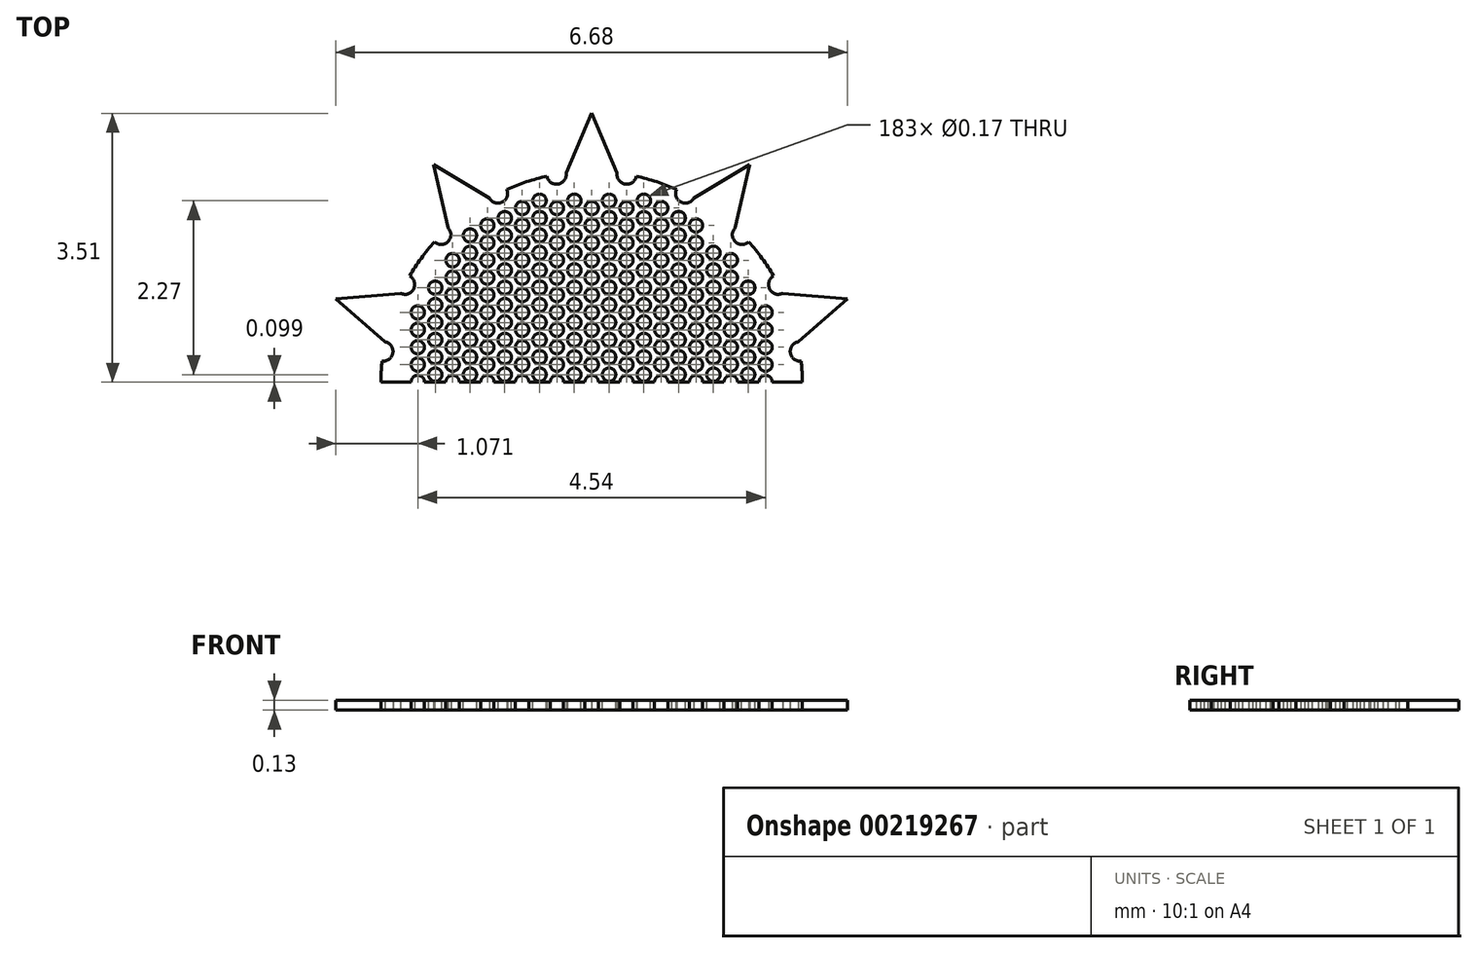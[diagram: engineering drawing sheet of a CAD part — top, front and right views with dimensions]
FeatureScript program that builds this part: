
annotation { "Feature Type Name" : "Feature", "Feature Type Description" : "" }
export const myFeature = defineFeature(function(context is Context, id is Id, definition is map)
    precondition{}
    {
        {
            var Q0;
            Q0=qCreatedBy(makeId("Top.planeOp"),FACE);
            var sketch = newSketch(context, id + "F0", { "sketchPlane" : qUnion([Q0])});
            skCircle(sketch, "E0", {"center": v(0, 0) * mm, "radius": 2.5 * mm});
            skArc(sketch, "E1", {"start": v(0.33, 2.73) * mm, "mid": v(0, 2.75) * mm, "end": v(-0.33, 2.73) * mm});
            skPoint(sketch, "E2", {"position": v(0, 2.75) * mm});
            skLineSegment(sketch, "E3", {"start": v(-3.94, 3.51) * mm, "end": v(3.7, 3.51) * mm, "construction": true});
            skLineSegment(sketch, "E4", {"start": v(0, 3.51) * mm, "end": v(-0.33, 2.73) * mm});
            skLineSegment(sketch, "E5", {"start": v(0, 3.51) * mm, "end": v(0.33, 2.73) * mm});
            skLineSegment(sketch, "E6.1.0", {"start": v(-2.06, 2.84) * mm, "end": v(-1.87, 2.01) * mm});
            skLineSegment(sketch, "E6.1.1", {"start": v(-2.06, 2.84) * mm, "end": v(-1.34, 2.4) * mm});
            skLineSegment(sketch, "E6.2.0", {"start": v(-3.34, 1.09) * mm, "end": v(-2.7, 0.53) * mm});
            skLineSegment(sketch, "E6.2.1", {"start": v(-3.34, 1.09) * mm, "end": v(-2.5, 1.16) * mm});
            skLineSegment(sketch, "E6.3.0", {"start": v(-3.34, -1.09) * mm, "end": v(-2.5, -1.16) * mm});
            skLineSegment(sketch, "E6.3.1", {"start": v(-3.34, -1.09) * mm, "end": v(-2.7, -0.53) * mm});
            skLineSegment(sketch, "E6.4.0", {"start": v(-2.06, -2.84) * mm, "end": v(-1.34, -2.4) * mm});
            skLineSegment(sketch, "E6.4.1", {"start": v(-2.06, -2.84) * mm, "end": v(-1.87, -2.01) * mm});
            skLineSegment(sketch, "E6.5.0", {"start": v(0, -3.51) * mm, "end": v(0.33, -2.73) * mm});
            skLineSegment(sketch, "E6.5.1", {"start": v(0, -3.51) * mm, "end": v(-0.33, -2.73) * mm});
            skLineSegment(sketch, "E6.6.0", {"start": v(2.06, -2.84) * mm, "end": v(1.87, -2.01) * mm});
            skLineSegment(sketch, "E6.6.1", {"start": v(2.06, -2.84) * mm, "end": v(1.34, -2.4) * mm});
            skLineSegment(sketch, "E6.7.0", {"start": v(3.34, -1.09) * mm, "end": v(2.7, -0.53) * mm});
            skLineSegment(sketch, "E6.7.1", {"start": v(3.34, -1.09) * mm, "end": v(2.5, -1.16) * mm});
            skLineSegment(sketch, "E6.8.0", {"start": v(3.34, 1.09) * mm, "end": v(2.5, 1.16) * mm});
            skLineSegment(sketch, "E6.8.1", {"start": v(3.34, 1.09) * mm, "end": v(2.7, 0.53) * mm});
            skLineSegment(sketch, "E6.9.0", {"start": v(2.06, 2.84) * mm, "end": v(1.34, 2.4) * mm});
            skLineSegment(sketch, "E6.9.1", {"start": v(2.06, 2.84) * mm, "end": v(1.87, 2.01) * mm});
            skCircle(sketch, "E7", {"center": v(0, 0) * mm, "radius": 2.62 * mm});
            skPoint(sketch, "E8", {"position": v(0.46, 2.71) * mm});
            skArc(sketch, "E9", {"start": v(0.33, 2.73) * mm, "mid": v(0.44, 2.59) * mm, "end": v(0.58, 2.69) * mm});
            skArc(sketch, "E10.1.0", {"start": v(-1.34, 2.4) * mm, "mid": v(-1.17, 2.35) * mm, "end": v(-1.1, 2.52) * mm});
            skArc(sketch, "E10.2.0", {"start": v(-2.5, 1.16) * mm, "mid": v(-2.32, 1.21) * mm, "end": v(-2.38, 1.38) * mm});
            skArc(sketch, "E10.3.0", {"start": v(-2.7, -0.53) * mm, "mid": v(-2.6, -0.38) * mm, "end": v(-2.74, -0.28) * mm});
            skArc(sketch, "E10.4.0", {"start": v(-1.87, -2.01) * mm, "mid": v(-1.87, -1.84) * mm, "end": v(-2.05, -1.83) * mm});
            skArc(sketch, "E10.5.0", {"start": v(-0.33, -2.73) * mm, "mid": v(-0.44, -2.59) * mm, "end": v(-0.58, -2.69) * mm});
            skArc(sketch, "E10.6.0", {"start": v(1.34, -2.4) * mm, "mid": v(1.17, -2.35) * mm, "end": v(1.1, -2.52) * mm});
            skArc(sketch, "E10.7.0", {"start": v(2.5, -1.16) * mm, "mid": v(2.32, -1.21) * mm, "end": v(2.38, -1.38) * mm});
            skArc(sketch, "E10.8.0", {"start": v(2.7, 0.53) * mm, "mid": v(2.6, 0.38) * mm, "end": v(2.74, 0.28) * mm});
            skArc(sketch, "E10.9.0", {"start": v(1.87, 2.01) * mm, "mid": v(1.87, 1.84) * mm, "end": v(2.05, 1.83) * mm});
            skArc(sketch, "E11", {"start": v(-0.58, 2.69) * mm, "mid": v(-0.44, 2.59) * mm, "end": v(-0.33, 2.73) * mm});
            skArc(sketch, "E12.trimOffspring", {"start": v(-0.58, 2.69) * mm, "mid": v(-0.85, 2.62) * mm, "end": v(-1.1, 2.52) * mm});
            skArc(sketch, "E13.1.0", {"start": v(-2.05, 1.83) * mm, "mid": v(-1.87, 1.84) * mm, "end": v(-1.87, 2.01) * mm});
            skArc(sketch, "E13.2.0", {"start": v(-2.74, 0.28) * mm, "mid": v(-2.6, 0.38) * mm, "end": v(-2.7, 0.53) * mm});
            skArc(sketch, "E13.3.0", {"start": v(-2.38, -1.38) * mm, "mid": v(-2.32, -1.21) * mm, "end": v(-2.5, -1.16) * mm});
            skArc(sketch, "E13.4.0", {"start": v(-1.1, -2.52) * mm, "mid": v(-1.17, -2.35) * mm, "end": v(-1.34, -2.4) * mm});
            skArc(sketch, "E13.5.0", {"start": v(0.58, -2.69) * mm, "mid": v(0.44, -2.59) * mm, "end": v(0.33, -2.73) * mm});
            skArc(sketch, "E13.6.0", {"start": v(2.05, -1.83) * mm, "mid": v(1.87, -1.84) * mm, "end": v(1.87, -2.01) * mm});
            skArc(sketch, "E13.7.0", {"start": v(2.74, -0.28) * mm, "mid": v(2.6, -0.38) * mm, "end": v(2.7, -0.53) * mm});
            skArc(sketch, "E13.8.0", {"start": v(2.38, 1.38) * mm, "mid": v(2.32, 1.21) * mm, "end": v(2.5, 1.16) * mm});
            skArc(sketch, "E13.9.0", {"start": v(1.1, 2.52) * mm, "mid": v(1.17, 2.35) * mm, "end": v(1.34, 2.4) * mm});
            skArc(sketch, "E14.trimOffspring", {"start": v(1.1, 2.52) * mm, "mid": v(0.85, 2.62) * mm, "end": v(0.58, 2.69) * mm});
            skArc(sketch, "E15.trimOffspring", {"start": v(1.87, 2.01) * mm, "mid": v(1.62, 2.22) * mm, "end": v(1.34, 2.4) * mm});
            skArc(sketch, "E16.trimOffspring", {"start": v(2.38, 1.38) * mm, "mid": v(2.22, 1.62) * mm, "end": v(2.05, 1.83) * mm});
            skArc(sketch, "E17.trimOffspring", {"start": v(2.7, 0.53) * mm, "mid": v(2.62, 0.85) * mm, "end": v(2.5, 1.16) * mm});
            skArc(sketch, "E18.trimOffspring", {"start": v(2.74, -0.28) * mm, "mid": v(2.75, 0) * mm, "end": v(2.74, 0.28) * mm});
            skArc(sketch, "E19.trimOffspring", {"start": v(2.5, -1.16) * mm, "mid": v(2.62, -0.85) * mm, "end": v(2.7, -0.53) * mm});
            skArc(sketch, "E20.trimOffspring", {"start": v(2.05, -1.83) * mm, "mid": v(2.22, -1.62) * mm, "end": v(2.38, -1.38) * mm});
            skArc(sketch, "E21.trimOffspring", {"start": v(1.34, -2.4) * mm, "mid": v(1.62, -2.22) * mm, "end": v(1.87, -2.01) * mm});
            skArc(sketch, "E22.trimOffspring", {"start": v(-2.38, -1.38) * mm, "mid": v(-2.22, -1.62) * mm, "end": v(-2.05, -1.83) * mm});
            skArc(sketch, "E23.trimOffspring", {"start": v(-1.87, -2.01) * mm, "mid": v(-1.62, -2.22) * mm, "end": v(-1.34, -2.4) * mm});
            skArc(sketch, "E24.trimOffspring", {"start": v(-1.1, -2.52) * mm, "mid": v(-0.85, -2.62) * mm, "end": v(-0.58, -2.69) * mm});
            skArc(sketch, "E25.trimOffspring", {"start": v(-0.33, -2.73) * mm, "mid": v(0, -2.75) * mm, "end": v(0.33, -2.73) * mm});
            skArc(sketch, "E26.trimOffspring", {"start": v(0.58, -2.69) * mm, "mid": v(0.85, -2.62) * mm, "end": v(1.1, -2.52) * mm});
            skArc(sketch, "E27.trimOffspring", {"start": v(-2.7, -0.53) * mm, "mid": v(-2.62, -0.85) * mm, "end": v(-2.5, -1.16) * mm});
            skArc(sketch, "E28.trimOffspring", {"start": v(-2.74, 0.28) * mm, "mid": v(-2.75, 0) * mm, "end": v(-2.74, -0.28) * mm});
            skArc(sketch, "E29.trimOffspring", {"start": v(-2.5, 1.16) * mm, "mid": v(-2.62, 0.85) * mm, "end": v(-2.7, 0.53) * mm});
            skArc(sketch, "E30.trimOffspring", {"start": v(-2.05, 1.83) * mm, "mid": v(-2.22, 1.62) * mm, "end": v(-2.38, 1.38) * mm});
            skArc(sketch, "E31.trimOffspring", {"start": v(-1.34, 2.4) * mm, "mid": v(-1.62, 2.22) * mm, "end": v(-1.87, 2.01) * mm});
            skSolve(sketch);
        }
        {
            var Q0;
            Q0=qSketchRegion(id+"F0",true);
            var Q1;
            Q1=makeQuery(id+"F0.imprint","IMPRINT",FACE,{"disambiguationData":[TD([[makeQuery(id+"F0.imprint","IMPRINT",EDGE,{"derivedFrom":sQuery(id+"F0.wireOp",EDGE,"E0")}),1.0]])]});
            extrude(context, id + "F1", {"entities" : qUnion([Q0, Q1]), "depth" : 0.13 * mm});
        }
        {
            var Q0;
            Q0=makeQuery(id+"F1.opExtrude","CAP_FACE",FACE,{"disambiguationData":[OSD([sQuery(id+"F0.wireOp",EDGE,"E1"),sQuery(id+"F0.wireOp",EDGE,"E4"),sQuery(id+"F0.wireOp",EDGE,"E5"),sQuery(id+"F0.wireOp",EDGE,"E6.1.0"),sQuery(id+"F0.wireOp",EDGE,"E6.1.1"),sQuery(id+"F0.wireOp",EDGE,"E6.2.0"),sQuery(id+"F0.wireOp",EDGE,"E6.2.1"),sQuery(id+"F0.wireOp",EDGE,"E6.3.0"),sQuery(id+"F0.wireOp",EDGE,"E6.3.1"),sQuery(id+"F0.wireOp",EDGE,"E6.4.0"),sQuery(id+"F0.wireOp",EDGE,"E6.4.1"),sQuery(id+"F0.wireOp",EDGE,"E6.5.0"),sQuery(id+"F0.wireOp",EDGE,"E6.5.1"),sQuery(id+"F0.wireOp",EDGE,"E6.6.0"),sQuery(id+"F0.wireOp",EDGE,"E6.6.1"),sQuery(id+"F0.wireOp",EDGE,"E6.7.0"),sQuery(id+"F0.wireOp",EDGE,"E6.7.1"),sQuery(id+"F0.wireOp",EDGE,"E6.8.0"),sQuery(id+"F0.wireOp",EDGE,"E6.8.1"),sQuery(id+"F0.wireOp",EDGE,"E6.9.0"),sQuery(id+"F0.wireOp",EDGE,"E6.9.1")])],"isStart":false});
            cPlane(context, id + "F2", {"entities" : qUnion([Q0]), "cplaneType" : CPlaneType.OFFSET, "offset" : 0 * mm, "width" : 150 * mm, "height" : 150 * mm});
        }
        {
            var Q0;
            Q0=qCreatedBy(id+"F2.planeOp",FACE);
            var sketch = newSketch(context, id + "F3", { "sketchPlane" : qUnion([Q0])});
            skCircle(sketch, "E32.2.1.8", {"center": v(-2.04, 1.23) * mm, "radius": 0.09 * mm});
            skCircle(sketch, "E32.2.1.9", {"center": v(-2.04, 1) * mm, "radius": 0.09 * mm});
            skCircle(sketch, "E32.0.1.10", {"center": v(-2.27, 0.91) * mm, "radius": 0.09 * mm});
            skCircle(sketch, "E32.2.1.10", {"center": v(-2.04, 0.78) * mm, "radius": 0.09 * mm});
            skCircle(sketch, "E32.2.2.5", {"center": v(-1.59, 1.91) * mm, "radius": 0.09 * mm});
            skCircle(sketch, "E32.2.2.6", {"center": v(-1.59, 1.69) * mm, "radius": 0.09 * mm});
            skCircle(sketch, "E32.0.2.7", {"center": v(-1.82, 1.6) * mm, "radius": 0.09 * mm});
            skCircle(sketch, "E32.2.2.7", {"center": v(-1.59, 1.46) * mm, "radius": 0.09 * mm});
            skCircle(sketch, "E32.0.2.8", {"center": v(-1.82, 1.36) * mm, "radius": 0.09 * mm});
            skCircle(sketch, "E32.2.2.8", {"center": v(-1.59, 1.23) * mm, "radius": 0.09 * mm});
            skCircle(sketch, "E32.0.2.9", {"center": v(-1.82, 1.14) * mm, "radius": 0.09 * mm});
            skCircle(sketch, "E32.2.2.9", {"center": v(-1.59, 1) * mm, "radius": 0.09 * mm});
            skCircle(sketch, "E32.0.2.10", {"center": v(-1.82, 0.91) * mm, "radius": 0.09 * mm});
            skCircle(sketch, "E32.2.2.10", {"center": v(-1.59, 0.78) * mm, "radius": 0.09 * mm});
            skCircle(sketch, "E32.2.3.4", {"center": v(-1.13, 2.14) * mm, "radius": 0.09 * mm});
            skCircle(sketch, "E32.0.3.5", {"center": v(-1.36, 2.05) * mm, "radius": 0.09 * mm});
            skCircle(sketch, "E32.2.3.5", {"center": v(-1.13, 1.91) * mm, "radius": 0.09 * mm});
            skCircle(sketch, "E32.0.3.6", {"center": v(-1.36, 1.82) * mm, "radius": 0.09 * mm});
            skCircle(sketch, "E32.2.3.6", {"center": v(-1.13, 1.69) * mm, "radius": 0.09 * mm});
            skCircle(sketch, "E32.0.3.7", {"center": v(-1.36, 1.6) * mm, "radius": 0.09 * mm});
            skCircle(sketch, "E32.2.3.7", {"center": v(-1.13, 1.46) * mm, "radius": 0.09 * mm});
            skCircle(sketch, "E32.0.3.8", {"center": v(-1.36, 1.36) * mm, "radius": 0.09 * mm});
            skCircle(sketch, "E32.2.3.8", {"center": v(-1.13, 1.23) * mm, "radius": 0.09 * mm});
            skCircle(sketch, "E32.0.3.9", {"center": v(-1.36, 1.14) * mm, "radius": 0.09 * mm});
            skCircle(sketch, "E32.2.3.9", {"center": v(-1.13, 1) * mm, "radius": 0.09 * mm});
            skCircle(sketch, "E32.0.3.10", {"center": v(-1.36, 0.91) * mm, "radius": 0.09 * mm});
            skCircle(sketch, "E32.2.3.10", {"center": v(-1.13, 0.78) * mm, "radius": 0.09 * mm});
            skCircle(sketch, "E32.2.4.3", {"center": v(-0.68, 2.37) * mm, "radius": 0.09 * mm});
            skCircle(sketch, "E32.0.4.4", {"center": v(-0.9, 2.27) * mm, "radius": 0.09 * mm});
            skCircle(sketch, "E32.2.4.4", {"center": v(-0.68, 2.14) * mm, "radius": 0.09 * mm});
            skCircle(sketch, "E32.0.4.5", {"center": v(-0.9, 2.05) * mm, "radius": 0.09 * mm});
            skCircle(sketch, "E32.2.4.5", {"center": v(-0.68, 1.91) * mm, "radius": 0.09 * mm});
            skCircle(sketch, "E32.0.4.6", {"center": v(-0.9, 1.82) * mm, "radius": 0.09 * mm});
            skCircle(sketch, "E32.2.4.6", {"center": v(-0.68, 1.69) * mm, "radius": 0.09 * mm});
            skCircle(sketch, "E32.0.4.7", {"center": v(-0.9, 1.6) * mm, "radius": 0.09 * mm});
            skCircle(sketch, "E32.2.4.7", {"center": v(-0.68, 1.46) * mm, "radius": 0.09 * mm});
            skCircle(sketch, "E32.0.4.8", {"center": v(-0.9, 1.36) * mm, "radius": 0.09 * mm});
            skCircle(sketch, "E32.2.4.8", {"center": v(-0.68, 1.23) * mm, "radius": 0.09 * mm});
            skCircle(sketch, "E32.0.4.9", {"center": v(-0.9, 1.14) * mm, "radius": 0.09 * mm});
            skCircle(sketch, "E32.2.4.9", {"center": v(-0.68, 1) * mm, "radius": 0.09 * mm});
            skCircle(sketch, "E32.0.4.10", {"center": v(-0.9, 0.91) * mm, "radius": 0.09 * mm});
            skCircle(sketch, "E32.2.4.10", {"center": v(-0.68, 0.78) * mm, "radius": 0.09 * mm});
            skCircle(sketch, "E32.2.5.3", {"center": v(-0.23, 2.37) * mm, "radius": 0.09 * mm});
            skCircle(sketch, "E32.0.5.4", {"center": v(-0.45, 2.27) * mm, "radius": 0.09 * mm});
            skCircle(sketch, "E32.2.5.4", {"center": v(-0.23, 2.14) * mm, "radius": 0.09 * mm});
            skCircle(sketch, "E32.0.5.5", {"center": v(-0.45, 2.05) * mm, "radius": 0.09 * mm});
            skCircle(sketch, "E32.2.5.5", {"center": v(-0.23, 1.91) * mm, "radius": 0.09 * mm});
            skCircle(sketch, "E32.0.5.6", {"center": v(-0.45, 1.82) * mm, "radius": 0.09 * mm});
            skCircle(sketch, "E32.2.5.6", {"center": v(-0.23, 1.69) * mm, "radius": 0.09 * mm});
            skCircle(sketch, "E32.0.5.7", {"center": v(-0.45, 1.6) * mm, "radius": 0.09 * mm});
            skCircle(sketch, "E32.2.5.7", {"center": v(-0.23, 1.46) * mm, "radius": 0.09 * mm});
            skCircle(sketch, "E32.0.5.8", {"center": v(-0.45, 1.36) * mm, "radius": 0.09 * mm});
            skCircle(sketch, "E32.2.5.8", {"center": v(-0.23, 1.23) * mm, "radius": 0.09 * mm});
            skCircle(sketch, "E32.0.5.9", {"center": v(-0.45, 1.14) * mm, "radius": 0.09 * mm});
            skCircle(sketch, "E32.2.5.9", {"center": v(-0.23, 1) * mm, "radius": 0.09 * mm});
            skCircle(sketch, "E32.0.5.10", {"center": v(-0.45, 0.91) * mm, "radius": 0.09 * mm});
            skCircle(sketch, "E32.2.5.10", {"center": v(-0.23, 0.78) * mm, "radius": 0.09 * mm});
            skCircle(sketch, "E32.2.6.3", {"center": v(0.23, 2.37) * mm, "radius": 0.09 * mm});
            skCircle(sketch, "E32.0.6.4", {"center": v(0, 2.27) * mm, "radius": 0.09 * mm});
            skCircle(sketch, "E32.2.6.4", {"center": v(0.23, 2.14) * mm, "radius": 0.09 * mm});
            skCircle(sketch, "E32.0.6.5", {"center": v(0, 2.05) * mm, "radius": 0.09 * mm});
            skCircle(sketch, "E32.2.6.5", {"center": v(0.23, 1.91) * mm, "radius": 0.09 * mm});
            skCircle(sketch, "E32.0.6.6", {"center": v(0, 1.82) * mm, "radius": 0.09 * mm});
            skCircle(sketch, "E32.2.6.6", {"center": v(0.23, 1.69) * mm, "radius": 0.09 * mm});
            skCircle(sketch, "E32.0.6.7", {"center": v(0, 1.6) * mm, "radius": 0.09 * mm});
            skCircle(sketch, "E32.2.6.7", {"center": v(0.23, 1.46) * mm, "radius": 0.09 * mm});
            skCircle(sketch, "E32.0.6.8", {"center": v(0, 1.36) * mm, "radius": 0.09 * mm});
            skCircle(sketch, "E32.2.6.8", {"center": v(0.23, 1.23) * mm, "radius": 0.09 * mm});
            skCircle(sketch, "E32.0.6.9", {"center": v(0, 1.14) * mm, "radius": 0.09 * mm});
            skCircle(sketch, "E32.2.6.9", {"center": v(0.23, 1) * mm, "radius": 0.09 * mm});
            skCircle(sketch, "E32.0.6.10", {"center": v(0, 0.91) * mm, "radius": 0.09 * mm});
            skCircle(sketch, "E32.2.6.10", {"center": v(0.23, 0.78) * mm, "radius": 0.09 * mm});
            skCircle(sketch, "E32.2.7.3", {"center": v(0.68, 2.37) * mm, "radius": 0.09 * mm});
            skCircle(sketch, "E32.0.7.4", {"center": v(0.45, 2.27) * mm, "radius": 0.09 * mm});
            skCircle(sketch, "E32.2.7.4", {"center": v(0.68, 2.14) * mm, "radius": 0.09 * mm});
            skCircle(sketch, "E32.0.7.5", {"center": v(0.45, 2.05) * mm, "radius": 0.09 * mm});
            skCircle(sketch, "E32.2.7.5", {"center": v(0.68, 1.91) * mm, "radius": 0.09 * mm});
            skCircle(sketch, "E32.0.7.6", {"center": v(0.45, 1.82) * mm, "radius": 0.09 * mm});
            skCircle(sketch, "E32.2.7.6", {"center": v(0.68, 1.69) * mm, "radius": 0.09 * mm});
            skCircle(sketch, "E32.0.7.7", {"center": v(0.45, 1.6) * mm, "radius": 0.09 * mm});
            skCircle(sketch, "E32.2.7.7", {"center": v(0.68, 1.46) * mm, "radius": 0.09 * mm});
            skCircle(sketch, "E32.0.7.8", {"center": v(0.45, 1.36) * mm, "radius": 0.09 * mm});
            skCircle(sketch, "E32.2.7.8", {"center": v(0.68, 1.23) * mm, "radius": 0.09 * mm});
            skCircle(sketch, "E32.0.7.9", {"center": v(0.45, 1.14) * mm, "radius": 0.09 * mm});
            skCircle(sketch, "E32.2.7.9", {"center": v(0.68, 1) * mm, "radius": 0.09 * mm});
            skCircle(sketch, "E32.0.7.10", {"center": v(0.45, 0.91) * mm, "radius": 0.09 * mm});
            skCircle(sketch, "E32.2.7.10", {"center": v(0.68, 0.78) * mm, "radius": 0.09 * mm});
            skCircle(sketch, "E32.0.8.4", {"center": v(0.9, 2.27) * mm, "radius": 0.09 * mm});
            skCircle(sketch, "E32.2.8.4", {"center": v(1.14, 2.14) * mm, "radius": 0.09 * mm});
            skCircle(sketch, "E32.0.8.5", {"center": v(0.9, 2.05) * mm, "radius": 0.09 * mm});
            skCircle(sketch, "E32.2.8.5", {"center": v(1.14, 1.91) * mm, "radius": 0.09 * mm});
            skCircle(sketch, "E32.0.8.6", {"center": v(0.9, 1.82) * mm, "radius": 0.09 * mm});
            skCircle(sketch, "E32.2.8.6", {"center": v(1.14, 1.69) * mm, "radius": 0.09 * mm});
            skCircle(sketch, "E32.0.8.7", {"center": v(0.9, 1.6) * mm, "radius": 0.09 * mm});
            skCircle(sketch, "E32.2.8.7", {"center": v(1.14, 1.46) * mm, "radius": 0.09 * mm});
            skCircle(sketch, "E32.0.8.8", {"center": v(0.9, 1.36) * mm, "radius": 0.09 * mm});
            skCircle(sketch, "E32.2.8.8", {"center": v(1.14, 1.23) * mm, "radius": 0.09 * mm});
            skCircle(sketch, "E32.0.8.9", {"center": v(0.9, 1.14) * mm, "radius": 0.09 * mm});
            skCircle(sketch, "E32.2.8.9", {"center": v(1.14, 1) * mm, "radius": 0.09 * mm});
            skCircle(sketch, "E32.0.8.10", {"center": v(0.9, 0.91) * mm, "radius": 0.09 * mm});
            skCircle(sketch, "E32.2.8.10", {"center": v(1.14, 0.78) * mm, "radius": 0.09 * mm});
            skCircle(sketch, "E32.0.9.5", {"center": v(1.36, 2.05) * mm, "radius": 0.09 * mm});
            skCircle(sketch, "E32.0.9.6", {"center": v(1.36, 1.82) * mm, "radius": 0.09 * mm});
            skCircle(sketch, "E32.2.9.6", {"center": v(1.6, 1.69) * mm, "radius": 0.09 * mm});
            skCircle(sketch, "E32.0.9.7", {"center": v(1.36, 1.6) * mm, "radius": 0.09 * mm});
            skCircle(sketch, "E32.2.9.7", {"center": v(1.6, 1.46) * mm, "radius": 0.09 * mm});
            skCircle(sketch, "E32.0.9.8", {"center": v(1.36, 1.36) * mm, "radius": 0.09 * mm});
            skCircle(sketch, "E32.2.9.8", {"center": v(1.6, 1.23) * mm, "radius": 0.09 * mm});
            skCircle(sketch, "E32.0.9.9", {"center": v(1.36, 1.14) * mm, "radius": 0.09 * mm});
            skCircle(sketch, "E32.2.9.9", {"center": v(1.6, 1) * mm, "radius": 0.09 * mm});
            skCircle(sketch, "E32.0.9.10", {"center": v(1.36, 0.91) * mm, "radius": 0.09 * mm});
            skCircle(sketch, "E32.2.9.10", {"center": v(1.6, 0.78) * mm, "radius": 0.09 * mm});
            skCircle(sketch, "E32.0.10.7", {"center": v(1.82, 1.6) * mm, "radius": 0.09 * mm});
            skCircle(sketch, "E32.0.10.8", {"center": v(1.82, 1.36) * mm, "radius": 0.09 * mm});
            skCircle(sketch, "E32.2.10.8", {"center": v(2.04, 1.23) * mm, "radius": 0.09 * mm});
            skCircle(sketch, "E32.0.10.9", {"center": v(1.82, 1.14) * mm, "radius": 0.09 * mm});
            skCircle(sketch, "E32.2.10.9", {"center": v(2.04, 1) * mm, "radius": 0.09 * mm});
            skCircle(sketch, "E32.0.10.10", {"center": v(1.82, 0.91) * mm, "radius": 0.09 * mm});
            skCircle(sketch, "E32.2.10.10", {"center": v(2.04, 0.78) * mm, "radius": 0.09 * mm});
            skCircle(sketch, "E33.0.1.11", {"center": v(-2.27, 0.68) * mm, "radius": 0.09 * mm});
            skCircle(sketch, "E33.2.1.11", {"center": v(-2.04, 0.55) * mm, "radius": 0.09 * mm});
            skCircle(sketch, "E33.0.1.12", {"center": v(-2.27, 0.46) * mm, "radius": 0.09 * mm});
            skCircle(sketch, "E33.2.1.12", {"center": v(-2.04, 0.33) * mm, "radius": 0.09 * mm});
            skCircle(sketch, "E33.0.1.13", {"center": v(-2.27, 0.23) * mm, "radius": 0.09 * mm});
            skCircle(sketch, "E33.2.1.13", {"center": v(-2.04, 0.1) * mm, "radius": 0.09 * mm});
            skCircle(sketch, "E33.0.1.14", {"center": v(-2.27, 0) * mm, "radius": 0.09 * mm});
            skCircle(sketch, "E33.2.1.14", {"center": v(-2.04, -0.13) * mm, "radius": 0.09 * mm});
            skCircle(sketch, "E33.0.1.15", {"center": v(-2.27, -0.22) * mm, "radius": 0.09 * mm});
            skCircle(sketch, "E33.2.1.15", {"center": v(-2.04, -0.36) * mm, "radius": 0.09 * mm});
            skCircle(sketch, "E33.0.1.16", {"center": v(-2.27, -0.45) * mm, "radius": 0.09 * mm});
            skCircle(sketch, "E33.2.1.16", {"center": v(-2.04, -0.58) * mm, "radius": 0.09 * mm});
            skCircle(sketch, "E33.0.1.17", {"center": v(-2.27, -0.68) * mm, "radius": 0.09 * mm});
            skCircle(sketch, "E33.2.1.17", {"center": v(-2.04, -0.8) * mm, "radius": 0.09 * mm});
            skCircle(sketch, "E33.0.1.18", {"center": v(-2.27, -0.9) * mm, "radius": 0.09 * mm});
            skCircle(sketch, "E33.2.1.18", {"center": v(-2.04, -1.04) * mm, "radius": 0.09 * mm});
            skCircle(sketch, "E33.2.1.19", {"center": v(-2.04, -1.26) * mm, "radius": 0.09 * mm});
            skCircle(sketch, "E33.0.2.11", {"center": v(-1.82, 0.68) * mm, "radius": 0.09 * mm});
            skCircle(sketch, "E33.2.2.11", {"center": v(-1.59, 0.55) * mm, "radius": 0.09 * mm});
            skCircle(sketch, "E33.0.2.12", {"center": v(-1.82, 0.46) * mm, "radius": 0.09 * mm});
            skCircle(sketch, "E33.2.2.12", {"center": v(-1.59, 0.33) * mm, "radius": 0.09 * mm});
            skCircle(sketch, "E33.0.2.13", {"center": v(-1.82, 0.23) * mm, "radius": 0.09 * mm});
            skCircle(sketch, "E33.2.2.13", {"center": v(-1.59, 0.1) * mm, "radius": 0.09 * mm});
            skCircle(sketch, "E33.0.2.14", {"center": v(-1.82, 0) * mm, "radius": 0.09 * mm});
            skCircle(sketch, "E33.2.2.14", {"center": v(-1.59, -0.13) * mm, "radius": 0.09 * mm});
            skCircle(sketch, "E33.0.2.15", {"center": v(-1.82, -0.22) * mm, "radius": 0.09 * mm});
            skCircle(sketch, "E33.2.2.15", {"center": v(-1.59, -0.36) * mm, "radius": 0.09 * mm});
            skCircle(sketch, "E33.0.2.16", {"center": v(-1.82, -0.45) * mm, "radius": 0.09 * mm});
            skCircle(sketch, "E33.2.2.16", {"center": v(-1.59, -0.58) * mm, "radius": 0.09 * mm});
            skCircle(sketch, "E33.0.2.17", {"center": v(-1.82, -0.68) * mm, "radius": 0.09 * mm});
            skCircle(sketch, "E33.2.2.17", {"center": v(-1.59, -0.8) * mm, "radius": 0.09 * mm});
            skCircle(sketch, "E33.0.2.18", {"center": v(-1.82, -0.9) * mm, "radius": 0.09 * mm});
            skCircle(sketch, "E33.2.2.18", {"center": v(-1.59, -1.04) * mm, "radius": 0.09 * mm});
            skCircle(sketch, "E33.0.2.19", {"center": v(-1.82, -1.13) * mm, "radius": 0.09 * mm});
            skCircle(sketch, "E33.2.2.19", {"center": v(-1.59, -1.26) * mm, "radius": 0.09 * mm});
            skCircle(sketch, "E33.0.2.20", {"center": v(-1.82, -1.36) * mm, "radius": 0.09 * mm});
            skCircle(sketch, "E33.2.2.20", {"center": v(-1.59, -1.5) * mm, "radius": 0.09 * mm});
            skCircle(sketch, "E33.0.2.21", {"center": v(-1.82, -1.59) * mm, "radius": 0.09 * mm});
            skCircle(sketch, "E33.2.2.21", {"center": v(-1.59, -1.72) * mm, "radius": 0.09 * mm});
            skCircle(sketch, "E33.0.3.11", {"center": v(-1.36, 0.68) * mm, "radius": 0.09 * mm});
            skCircle(sketch, "E33.2.3.11", {"center": v(-1.13, 0.55) * mm, "radius": 0.09 * mm});
            skCircle(sketch, "E33.0.3.12", {"center": v(-1.36, 0.46) * mm, "radius": 0.09 * mm});
            skCircle(sketch, "E33.2.3.12", {"center": v(-1.13, 0.33) * mm, "radius": 0.09 * mm});
            skCircle(sketch, "E33.0.3.13", {"center": v(-1.36, 0.23) * mm, "radius": 0.09 * mm});
            skCircle(sketch, "E33.2.3.13", {"center": v(-1.13, 0.1) * mm, "radius": 0.09 * mm});
            skCircle(sketch, "E33.0.3.14", {"center": v(-1.36, 0) * mm, "radius": 0.09 * mm});
            skCircle(sketch, "E33.2.3.14", {"center": v(-1.13, -0.13) * mm, "radius": 0.09 * mm});
            skCircle(sketch, "E33.0.3.15", {"center": v(-1.36, -0.22) * mm, "radius": 0.09 * mm});
            skCircle(sketch, "E33.2.3.15", {"center": v(-1.13, -0.36) * mm, "radius": 0.09 * mm});
            skCircle(sketch, "E33.0.3.16", {"center": v(-1.36, -0.45) * mm, "radius": 0.09 * mm});
            skCircle(sketch, "E33.2.3.16", {"center": v(-1.13, -0.58) * mm, "radius": 0.09 * mm});
            skCircle(sketch, "E33.0.3.17", {"center": v(-1.36, -0.68) * mm, "radius": 0.09 * mm});
            skCircle(sketch, "E33.2.3.17", {"center": v(-1.13, -0.8) * mm, "radius": 0.09 * mm});
            skCircle(sketch, "E33.0.3.18", {"center": v(-1.36, -0.9) * mm, "radius": 0.09 * mm});
            skCircle(sketch, "E33.2.3.18", {"center": v(-1.13, -1.04) * mm, "radius": 0.09 * mm});
            skCircle(sketch, "E33.0.3.19", {"center": v(-1.36, -1.13) * mm, "radius": 0.09 * mm});
            skCircle(sketch, "E33.2.3.19", {"center": v(-1.13, -1.26) * mm, "radius": 0.09 * mm});
            skCircle(sketch, "E33.0.3.20", {"center": v(-1.36, -1.36) * mm, "radius": 0.09 * mm});
            skCircle(sketch, "E33.2.3.20", {"center": v(-1.13, -1.5) * mm, "radius": 0.09 * mm});
            skCircle(sketch, "E33.0.3.21", {"center": v(-1.36, -1.59) * mm, "radius": 0.09 * mm});
            skCircle(sketch, "E33.2.3.21", {"center": v(-1.13, -1.72) * mm, "radius": 0.09 * mm});
            skCircle(sketch, "E33.0.4.11", {"center": v(-0.9, 0.68) * mm, "radius": 0.09 * mm});
            skCircle(sketch, "E33.2.4.11", {"center": v(-0.68, 0.55) * mm, "radius": 0.09 * mm});
            skCircle(sketch, "E33.0.4.12", {"center": v(-0.9, 0.46) * mm, "radius": 0.09 * mm});
            skCircle(sketch, "E33.2.4.12", {"center": v(-0.68, 0.33) * mm, "radius": 0.09 * mm});
            skCircle(sketch, "E33.0.4.13", {"center": v(-0.9, 0.23) * mm, "radius": 0.09 * mm});
            skCircle(sketch, "E33.2.4.13", {"center": v(-0.68, 0.1) * mm, "radius": 0.09 * mm});
            skCircle(sketch, "E33.0.4.14", {"center": v(-0.9, 0) * mm, "radius": 0.09 * mm});
            skCircle(sketch, "E33.2.4.14", {"center": v(-0.68, -0.13) * mm, "radius": 0.09 * mm});
            skCircle(sketch, "E33.0.4.15", {"center": v(-0.9, -0.22) * mm, "radius": 0.09 * mm});
            skCircle(sketch, "E33.2.4.15", {"center": v(-0.68, -0.36) * mm, "radius": 0.09 * mm});
            skCircle(sketch, "E33.0.4.16", {"center": v(-0.9, -0.45) * mm, "radius": 0.09 * mm});
            skCircle(sketch, "E33.2.4.16", {"center": v(-0.68, -0.58) * mm, "radius": 0.09 * mm});
            skCircle(sketch, "E33.0.4.17", {"center": v(-0.9, -0.68) * mm, "radius": 0.09 * mm});
            skCircle(sketch, "E33.2.4.17", {"center": v(-0.68, -0.8) * mm, "radius": 0.09 * mm});
            skCircle(sketch, "E33.0.4.18", {"center": v(-0.9, -0.9) * mm, "radius": 0.09 * mm});
            skCircle(sketch, "E33.2.4.18", {"center": v(-0.68, -1.04) * mm, "radius": 0.09 * mm});
            skCircle(sketch, "E33.0.4.19", {"center": v(-0.9, -1.13) * mm, "radius": 0.09 * mm});
            skCircle(sketch, "E33.2.4.19", {"center": v(-0.68, -1.26) * mm, "radius": 0.09 * mm});
            skCircle(sketch, "E33.0.4.20", {"center": v(-0.9, -1.36) * mm, "radius": 0.09 * mm});
            skCircle(sketch, "E33.2.4.20", {"center": v(-0.68, -1.5) * mm, "radius": 0.09 * mm});
            skCircle(sketch, "E33.0.4.21", {"center": v(-0.9, -1.59) * mm, "radius": 0.09 * mm});
            skCircle(sketch, "E33.2.4.21", {"center": v(-0.68, -1.72) * mm, "radius": 0.09 * mm});
            skCircle(sketch, "E33.0.5.11", {"center": v(-0.45, 0.68) * mm, "radius": 0.09 * mm});
            skCircle(sketch, "E33.2.5.11", {"center": v(-0.23, 0.55) * mm, "radius": 0.09 * mm});
            skCircle(sketch, "E33.0.5.12", {"center": v(-0.45, 0.46) * mm, "radius": 0.09 * mm});
            skCircle(sketch, "E33.2.5.12", {"center": v(-0.23, 0.33) * mm, "radius": 0.09 * mm});
            skCircle(sketch, "E33.0.5.13", {"center": v(-0.45, 0.23) * mm, "radius": 0.09 * mm});
            skCircle(sketch, "E33.2.5.13", {"center": v(-0.23, 0.1) * mm, "radius": 0.09 * mm});
            skCircle(sketch, "E33.0.5.14", {"center": v(-0.45, 0) * mm, "radius": 0.09 * mm});
            skCircle(sketch, "E33.2.5.14", {"center": v(-0.23, -0.13) * mm, "radius": 0.09 * mm});
            skCircle(sketch, "E33.0.5.15", {"center": v(-0.45, -0.22) * mm, "radius": 0.09 * mm});
            skCircle(sketch, "E33.2.5.15", {"center": v(-0.23, -0.36) * mm, "radius": 0.09 * mm});
            skCircle(sketch, "E33.0.5.16", {"center": v(-0.45, -0.45) * mm, "radius": 0.09 * mm});
            skCircle(sketch, "E33.2.5.16", {"center": v(-0.23, -0.58) * mm, "radius": 0.09 * mm});
            skCircle(sketch, "E33.0.5.17", {"center": v(-0.45, -0.68) * mm, "radius": 0.09 * mm});
            skCircle(sketch, "E33.2.5.17", {"center": v(-0.23, -0.8) * mm, "radius": 0.09 * mm});
            skCircle(sketch, "E33.0.5.18", {"center": v(-0.45, -0.9) * mm, "radius": 0.09 * mm});
            skCircle(sketch, "E33.2.5.18", {"center": v(-0.23, -1.04) * mm, "radius": 0.09 * mm});
            skCircle(sketch, "E33.0.5.19", {"center": v(-0.45, -1.13) * mm, "radius": 0.09 * mm});
            skCircle(sketch, "E33.2.5.19", {"center": v(-0.23, -1.26) * mm, "radius": 0.09 * mm});
            skCircle(sketch, "E33.0.5.20", {"center": v(-0.45, -1.36) * mm, "radius": 0.09 * mm});
            skCircle(sketch, "E33.2.5.20", {"center": v(-0.23, -1.5) * mm, "radius": 0.09 * mm});
            skCircle(sketch, "E33.0.5.21", {"center": v(-0.45, -1.59) * mm, "radius": 0.09 * mm});
            skCircle(sketch, "E33.2.5.21", {"center": v(-0.23, -1.72) * mm, "radius": 0.09 * mm});
            skCircle(sketch, "E33.0.6.11", {"center": v(0, 0.68) * mm, "radius": 0.09 * mm});
            skCircle(sketch, "E33.2.6.11", {"center": v(0.23, 0.55) * mm, "radius": 0.09 * mm});
            skCircle(sketch, "E33.0.6.12", {"center": v(0, 0.46) * mm, "radius": 0.09 * mm});
            skCircle(sketch, "E33.2.6.12", {"center": v(0.23, 0.33) * mm, "radius": 0.09 * mm});
            skCircle(sketch, "E33.0.6.13", {"center": v(0, 0.23) * mm, "radius": 0.09 * mm});
            skCircle(sketch, "E33.2.6.13", {"center": v(0.23, 0.1) * mm, "radius": 0.09 * mm});
            skCircle(sketch, "E33.0.6.14", {"center": v(0, 0) * mm, "radius": 0.09 * mm});
            skCircle(sketch, "E33.2.6.14", {"center": v(0.23, -0.13) * mm, "radius": 0.09 * mm});
            skCircle(sketch, "E33.0.6.15", {"center": v(0, -0.22) * mm, "radius": 0.09 * mm});
            skCircle(sketch, "E33.2.6.15", {"center": v(0.23, -0.36) * mm, "radius": 0.09 * mm});
            skCircle(sketch, "E33.0.6.16", {"center": v(0, -0.45) * mm, "radius": 0.09 * mm});
            skCircle(sketch, "E33.2.6.16", {"center": v(0.23, -0.58) * mm, "radius": 0.09 * mm});
            skCircle(sketch, "E33.0.6.17", {"center": v(0, -0.68) * mm, "radius": 0.09 * mm});
            skCircle(sketch, "E33.2.6.17", {"center": v(0.23, -0.8) * mm, "radius": 0.09 * mm});
            skCircle(sketch, "E33.0.6.18", {"center": v(0, -0.9) * mm, "radius": 0.09 * mm});
            skCircle(sketch, "E33.2.6.18", {"center": v(0.23, -1.04) * mm, "radius": 0.09 * mm});
            skCircle(sketch, "E33.0.6.19", {"center": v(0, -1.13) * mm, "radius": 0.09 * mm});
            skCircle(sketch, "E33.2.6.19", {"center": v(0.23, -1.26) * mm, "radius": 0.09 * mm});
            skCircle(sketch, "E33.0.6.20", {"center": v(0, -1.36) * mm, "radius": 0.09 * mm});
            skCircle(sketch, "E33.2.6.20", {"center": v(0.23, -1.5) * mm, "radius": 0.09 * mm});
            skCircle(sketch, "E33.0.6.21", {"center": v(0, -1.59) * mm, "radius": 0.09 * mm});
            skCircle(sketch, "E33.2.6.21", {"center": v(0.23, -1.72) * mm, "radius": 0.09 * mm});
            skCircle(sketch, "E33.0.7.11", {"center": v(0.45, 0.68) * mm, "radius": 0.09 * mm});
            skCircle(sketch, "E33.2.7.11", {"center": v(0.68, 0.55) * mm, "radius": 0.09 * mm});
            skCircle(sketch, "E33.0.7.12", {"center": v(0.45, 0.46) * mm, "radius": 0.09 * mm});
            skCircle(sketch, "E33.2.7.12", {"center": v(0.68, 0.33) * mm, "radius": 0.09 * mm});
            skCircle(sketch, "E33.0.7.13", {"center": v(0.45, 0.23) * mm, "radius": 0.09 * mm});
            skCircle(sketch, "E33.2.7.13", {"center": v(0.68, 0.1) * mm, "radius": 0.09 * mm});
            skCircle(sketch, "E33.0.7.14", {"center": v(0.45, 0) * mm, "radius": 0.09 * mm});
            skCircle(sketch, "E33.2.7.14", {"center": v(0.68, -0.13) * mm, "radius": 0.09 * mm});
            skCircle(sketch, "E33.0.7.15", {"center": v(0.45, -0.22) * mm, "radius": 0.09 * mm});
            skCircle(sketch, "E33.2.7.15", {"center": v(0.68, -0.36) * mm, "radius": 0.09 * mm});
            skCircle(sketch, "E33.0.7.16", {"center": v(0.45, -0.45) * mm, "radius": 0.09 * mm});
            skCircle(sketch, "E33.2.7.16", {"center": v(0.68, -0.58) * mm, "radius": 0.09 * mm});
            skCircle(sketch, "E33.0.7.17", {"center": v(0.45, -0.68) * mm, "radius": 0.09 * mm});
            skCircle(sketch, "E33.2.7.17", {"center": v(0.68, -0.8) * mm, "radius": 0.09 * mm});
            skCircle(sketch, "E33.0.7.18", {"center": v(0.45, -0.9) * mm, "radius": 0.09 * mm});
            skCircle(sketch, "E33.2.7.18", {"center": v(0.68, -1.04) * mm, "radius": 0.09 * mm});
            skCircle(sketch, "E33.0.7.19", {"center": v(0.45, -1.13) * mm, "radius": 0.09 * mm});
            skCircle(sketch, "E33.2.7.19", {"center": v(0.68, -1.26) * mm, "radius": 0.09 * mm});
            skCircle(sketch, "E33.0.7.20", {"center": v(0.45, -1.36) * mm, "radius": 0.09 * mm});
            skCircle(sketch, "E33.2.7.20", {"center": v(0.68, -1.5) * mm, "radius": 0.09 * mm});
            skCircle(sketch, "E33.0.7.21", {"center": v(0.45, -1.59) * mm, "radius": 0.09 * mm});
            skCircle(sketch, "E33.2.7.21", {"center": v(0.68, -1.72) * mm, "radius": 0.09 * mm});
            skCircle(sketch, "E33.0.8.11", {"center": v(0.9, 0.68) * mm, "radius": 0.09 * mm});
            skCircle(sketch, "E33.2.8.11", {"center": v(1.14, 0.55) * mm, "radius": 0.09 * mm});
            skCircle(sketch, "E33.0.8.12", {"center": v(0.9, 0.46) * mm, "radius": 0.09 * mm});
            skCircle(sketch, "E33.2.8.12", {"center": v(1.14, 0.33) * mm, "radius": 0.09 * mm});
            skCircle(sketch, "E33.0.8.13", {"center": v(0.9, 0.23) * mm, "radius": 0.09 * mm});
            skCircle(sketch, "E33.2.8.13", {"center": v(1.14, 0.1) * mm, "radius": 0.09 * mm});
            skCircle(sketch, "E33.0.8.14", {"center": v(0.9, 0) * mm, "radius": 0.09 * mm});
            skCircle(sketch, "E33.2.8.14", {"center": v(1.14, -0.13) * mm, "radius": 0.09 * mm});
            skCircle(sketch, "E33.0.8.15", {"center": v(0.9, -0.22) * mm, "radius": 0.09 * mm});
            skCircle(sketch, "E33.2.8.15", {"center": v(1.14, -0.36) * mm, "radius": 0.09 * mm});
            skCircle(sketch, "E33.0.8.16", {"center": v(0.9, -0.45) * mm, "radius": 0.09 * mm});
            skCircle(sketch, "E33.2.8.16", {"center": v(1.14, -0.58) * mm, "radius": 0.09 * mm});
            skCircle(sketch, "E33.0.8.17", {"center": v(0.9, -0.68) * mm, "radius": 0.09 * mm});
            skCircle(sketch, "E33.2.8.17", {"center": v(1.14, -0.8) * mm, "radius": 0.09 * mm});
            skCircle(sketch, "E33.0.8.18", {"center": v(0.9, -0.9) * mm, "radius": 0.09 * mm});
            skCircle(sketch, "E33.2.8.18", {"center": v(1.14, -1.04) * mm, "radius": 0.09 * mm});
            skCircle(sketch, "E33.0.8.19", {"center": v(0.9, -1.13) * mm, "radius": 0.09 * mm});
            skCircle(sketch, "E33.2.8.19", {"center": v(1.14, -1.26) * mm, "radius": 0.09 * mm});
            skCircle(sketch, "E33.0.8.20", {"center": v(0.9, -1.36) * mm, "radius": 0.09 * mm});
            skCircle(sketch, "E33.2.8.20", {"center": v(1.14, -1.5) * mm, "radius": 0.09 * mm});
            skCircle(sketch, "E33.0.8.21", {"center": v(0.9, -1.59) * mm, "radius": 0.09 * mm});
            skCircle(sketch, "E33.2.8.21", {"center": v(1.14, -1.72) * mm, "radius": 0.09 * mm});
            skCircle(sketch, "E33.0.9.11", {"center": v(1.36, 0.68) * mm, "radius": 0.09 * mm});
            skCircle(sketch, "E33.2.9.11", {"center": v(1.6, 0.55) * mm, "radius": 0.09 * mm});
            skCircle(sketch, "E33.0.9.12", {"center": v(1.36, 0.46) * mm, "radius": 0.09 * mm});
            skCircle(sketch, "E33.2.9.12", {"center": v(1.6, 0.33) * mm, "radius": 0.09 * mm});
            skCircle(sketch, "E33.0.9.13", {"center": v(1.36, 0.23) * mm, "radius": 0.09 * mm});
            skCircle(sketch, "E33.2.9.13", {"center": v(1.6, 0.1) * mm, "radius": 0.09 * mm});
            skCircle(sketch, "E33.0.9.14", {"center": v(1.36, 0) * mm, "radius": 0.09 * mm});
            skCircle(sketch, "E33.2.9.14", {"center": v(1.6, -0.13) * mm, "radius": 0.09 * mm});
            skCircle(sketch, "E33.0.9.15", {"center": v(1.36, -0.22) * mm, "radius": 0.09 * mm});
            skCircle(sketch, "E33.2.9.15", {"center": v(1.6, -0.36) * mm, "radius": 0.09 * mm});
            skCircle(sketch, "E33.0.9.16", {"center": v(1.36, -0.45) * mm, "radius": 0.09 * mm});
            skCircle(sketch, "E33.2.9.16", {"center": v(1.6, -0.58) * mm, "radius": 0.09 * mm});
            skCircle(sketch, "E33.0.9.17", {"center": v(1.36, -0.68) * mm, "radius": 0.09 * mm});
            skCircle(sketch, "E33.2.9.17", {"center": v(1.6, -0.8) * mm, "radius": 0.09 * mm});
            skCircle(sketch, "E33.0.9.18", {"center": v(1.36, -0.9) * mm, "radius": 0.09 * mm});
            skCircle(sketch, "E33.2.9.18", {"center": v(1.6, -1.04) * mm, "radius": 0.09 * mm});
            skCircle(sketch, "E33.0.9.19", {"center": v(1.36, -1.13) * mm, "radius": 0.09 * mm});
            skCircle(sketch, "E33.2.9.19", {"center": v(1.6, -1.26) * mm, "radius": 0.09 * mm});
            skCircle(sketch, "E33.0.9.20", {"center": v(1.36, -1.36) * mm, "radius": 0.09 * mm});
            skCircle(sketch, "E33.2.9.20", {"center": v(1.6, -1.5) * mm, "radius": 0.09 * mm});
            skCircle(sketch, "E33.0.9.21", {"center": v(1.36, -1.59) * mm, "radius": 0.09 * mm});
            skCircle(sketch, "E33.2.9.21", {"center": v(1.6, -1.72) * mm, "radius": 0.09 * mm});
            skCircle(sketch, "E33.0.10.11", {"center": v(1.82, 0.68) * mm, "radius": 0.09 * mm});
            skCircle(sketch, "E33.2.10.11", {"center": v(2.04, 0.55) * mm, "radius": 0.09 * mm});
            skCircle(sketch, "E33.0.10.12", {"center": v(1.82, 0.46) * mm, "radius": 0.09 * mm});
            skCircle(sketch, "E33.2.10.12", {"center": v(2.04, 0.33) * mm, "radius": 0.09 * mm});
            skCircle(sketch, "E33.0.10.13", {"center": v(1.82, 0.23) * mm, "radius": 0.09 * mm});
            skCircle(sketch, "E33.2.10.13", {"center": v(2.04, 0.1) * mm, "radius": 0.09 * mm});
            skCircle(sketch, "E33.0.10.14", {"center": v(1.82, 0) * mm, "radius": 0.09 * mm});
            skCircle(sketch, "E33.2.10.14", {"center": v(2.04, -0.13) * mm, "radius": 0.09 * mm});
            skCircle(sketch, "E33.0.10.15", {"center": v(1.82, -0.22) * mm, "radius": 0.09 * mm});
            skCircle(sketch, "E33.2.10.15", {"center": v(2.04, -0.36) * mm, "radius": 0.09 * mm});
            skCircle(sketch, "E33.0.10.16", {"center": v(1.82, -0.45) * mm, "radius": 0.09 * mm});
            skCircle(sketch, "E33.2.10.16", {"center": v(2.04, -0.58) * mm, "radius": 0.09 * mm});
            skCircle(sketch, "E33.0.10.17", {"center": v(1.82, -0.68) * mm, "radius": 0.09 * mm});
            skCircle(sketch, "E33.2.10.17", {"center": v(2.04, -0.8) * mm, "radius": 0.09 * mm});
            skCircle(sketch, "E33.0.10.18", {"center": v(1.82, -0.9) * mm, "radius": 0.09 * mm});
            skCircle(sketch, "E33.2.10.18", {"center": v(2.04, -1.04) * mm, "radius": 0.09 * mm});
            skCircle(sketch, "E33.0.10.19", {"center": v(1.82, -1.13) * mm, "radius": 0.09 * mm});
            skCircle(sketch, "E33.2.10.19", {"center": v(2.04, -1.26) * mm, "radius": 0.09 * mm});
            skCircle(sketch, "E33.0.10.20", {"center": v(1.82, -1.36) * mm, "radius": 0.09 * mm});
            skCircle(sketch, "E33.0.10.21", {"center": v(1.82, -1.59) * mm, "radius": 0.09 * mm});
            skCircle(sketch, "E34.0.11.10", {"center": v(2.27, 0.91) * mm, "radius": 0.09 * mm});
            skCircle(sketch, "E34.0.11.11", {"center": v(2.27, 0.68) * mm, "radius": 0.09 * mm});
            skCircle(sketch, "E34.0.11.12", {"center": v(2.27, 0.46) * mm, "radius": 0.09 * mm});
            skCircle(sketch, "E34.0.11.13", {"center": v(2.27, 0.23) * mm, "radius": 0.09 * mm});
            skCircle(sketch, "E34.0.11.14", {"center": v(2.27, 0) * mm, "radius": 0.09 * mm});
            skCircle(sketch, "E34.0.11.15", {"center": v(2.27, -0.22) * mm, "radius": 0.09 * mm});
            skCircle(sketch, "E34.0.11.16", {"center": v(2.27, -0.45) * mm, "radius": 0.09 * mm});
            skCircle(sketch, "E34.0.11.17", {"center": v(2.27, -0.68) * mm, "radius": 0.09 * mm});
            skCircle(sketch, "E34.0.11.18", {"center": v(2.27, -0.9) * mm, "radius": 0.09 * mm});
            skCircle(sketch, "E35.0.3.22", {"center": v(-1.36, -1.81) * mm, "radius": 0.09 * mm});
            skCircle(sketch, "E35.2.3.22", {"center": v(-1.13, -1.94) * mm, "radius": 0.09 * mm});
            skCircle(sketch, "E35.0.3.23", {"center": v(-1.36, -2.04) * mm, "radius": 0.09 * mm});
            skCircle(sketch, "E35.2.3.23", {"center": v(-1.13, -2.17) * mm, "radius": 0.09 * mm});
            skCircle(sketch, "E35.0.4.22", {"center": v(-0.9, -1.81) * mm, "radius": 0.09 * mm});
            skCircle(sketch, "E35.2.4.22", {"center": v(-0.68, -1.94) * mm, "radius": 0.09 * mm});
            skCircle(sketch, "E35.0.4.23", {"center": v(-0.9, -2.04) * mm, "radius": 0.09 * mm});
            skCircle(sketch, "E35.2.4.23", {"center": v(-0.68, -2.17) * mm, "radius": 0.09 * mm});
            skCircle(sketch, "E35.0.4.24", {"center": v(-0.9, -2.27) * mm, "radius": 0.09 * mm});
            skCircle(sketch, "E35.0.5.22", {"center": v(-0.45, -1.81) * mm, "radius": 0.09 * mm});
            skCircle(sketch, "E35.2.5.22", {"center": v(-0.23, -1.94) * mm, "radius": 0.09 * mm});
            skCircle(sketch, "E35.0.5.23", {"center": v(-0.45, -2.04) * mm, "radius": 0.09 * mm});
            skCircle(sketch, "E35.2.5.23", {"center": v(-0.23, -2.17) * mm, "radius": 0.09 * mm});
            skCircle(sketch, "E35.0.5.24", {"center": v(-0.45, -2.27) * mm, "radius": 0.09 * mm});
            skCircle(sketch, "E35.2.5.24", {"center": v(-0.23, -2.4) * mm, "radius": 0.09 * mm});
            skCircle(sketch, "E35.0.6.22", {"center": v(0, -1.81) * mm, "radius": 0.09 * mm});
            skCircle(sketch, "E35.2.6.22", {"center": v(0.23, -1.94) * mm, "radius": 0.09 * mm});
            skCircle(sketch, "E35.0.6.23", {"center": v(0, -2.04) * mm, "radius": 0.09 * mm});
            skCircle(sketch, "E35.2.6.23", {"center": v(0.23, -2.17) * mm, "radius": 0.09 * mm});
            skCircle(sketch, "E35.0.6.24", {"center": v(0, -2.27) * mm, "radius": 0.09 * mm});
            skCircle(sketch, "E35.2.6.24", {"center": v(0.23, -2.4) * mm, "radius": 0.09 * mm});
            skCircle(sketch, "E35.0.7.22", {"center": v(0.45, -1.81) * mm, "radius": 0.09 * mm});
            skCircle(sketch, "E35.2.7.22", {"center": v(0.68, -1.94) * mm, "radius": 0.09 * mm});
            skCircle(sketch, "E35.0.7.23", {"center": v(0.45, -2.04) * mm, "radius": 0.09 * mm});
            skCircle(sketch, "E35.2.7.23", {"center": v(0.68, -2.17) * mm, "radius": 0.09 * mm});
            skCircle(sketch, "E35.0.7.24", {"center": v(0.45, -2.27) * mm, "radius": 0.09 * mm});
            skCircle(sketch, "E35.0.8.22", {"center": v(0.9, -1.81) * mm, "radius": 0.09 * mm});
            skCircle(sketch, "E35.2.8.22", {"center": v(1.14, -1.94) * mm, "radius": 0.09 * mm});
            skCircle(sketch, "E35.0.8.23", {"center": v(0.9, -2.04) * mm, "radius": 0.09 * mm});
            skCircle(sketch, "E35.2.8.23", {"center": v(1.14, -2.17) * mm, "radius": 0.09 * mm});
            skCircle(sketch, "E35.0.8.24", {"center": v(0.9, -2.27) * mm, "radius": 0.09 * mm});
            skCircle(sketch, "E35.0.9.22", {"center": v(1.36, -1.81) * mm, "radius": 0.09 * mm});
            skCircle(sketch, "E35.0.9.23", {"center": v(1.36, -2.04) * mm, "radius": 0.09 * mm});
            skCircle(sketch, "E36.0", {"center": v(0, 0) * mm, "radius": 2.5 * mm, "construction": true});
            skSolve(sketch);
        }
        {
            var Q0;
            Q0=qSketchRegion(id+"F3",true);
            extrude(context, id + "F4", {"entities" : qUnion([Q0]), "operationType" : NewBodyOperationType.REMOVE, "endBound" : BoundingType.THROUGH_ALL, "oppositeDirection" : true, "depth" : 25 * mm});
        }
        {
            var Q0;
            Q0=makeQuery(id+"F1.opExtrude","CAP_FACE",FACE,{"disambiguationData":[OSD([sQuery(id+"F0.wireOp",EDGE,"E4"),sQuery(id+"F0.wireOp",EDGE,"E5"),sQuery(id+"F0.wireOp",EDGE,"E6.1.0"),sQuery(id+"F0.wireOp",EDGE,"E6.1.1"),sQuery(id+"F0.wireOp",EDGE,"E6.2.0"),sQuery(id+"F0.wireOp",EDGE,"E6.2.1"),sQuery(id+"F0.wireOp",EDGE,"E6.3.0"),sQuery(id+"F0.wireOp",EDGE,"E6.3.1"),sQuery(id+"F0.wireOp",EDGE,"E6.4.0"),sQuery(id+"F0.wireOp",EDGE,"E6.4.1"),sQuery(id+"F0.wireOp",EDGE,"E6.5.0"),sQuery(id+"F0.wireOp",EDGE,"E6.5.1"),sQuery(id+"F0.wireOp",EDGE,"E6.6.0"),sQuery(id+"F0.wireOp",EDGE,"E6.6.1"),sQuery(id+"F0.wireOp",EDGE,"E6.7.0"),sQuery(id+"F0.wireOp",EDGE,"E6.7.1"),sQuery(id+"F0.wireOp",EDGE,"E6.8.0"),sQuery(id+"F0.wireOp",EDGE,"E6.8.1"),sQuery(id+"F0.wireOp",EDGE,"E6.9.0"),sQuery(id+"F0.wireOp",EDGE,"E6.9.1"),sQuery(id+"F0.wireOp",EDGE,"E9"),sQuery(id+"F0.wireOp",EDGE,"E10.1.0"),sQuery(id+"F0.wireOp",EDGE,"E10.2.0"),sQuery(id+"F0.wireOp",EDGE,"E10.3.0"),sQuery(id+"F0.wireOp",EDGE,"E10.4.0"),sQuery(id+"F0.wireOp",EDGE,"E10.5.0"),sQuery(id+"F0.wireOp",EDGE,"E10.6.0"),sQuery(id+"F0.wireOp",EDGE,"E10.7.0"),sQuery(id+"F0.wireOp",EDGE,"E10.8.0"),sQuery(id+"F0.wireOp",EDGE,"E10.9.0"),sQuery(id+"F0.wireOp",EDGE,"E11"),sQuery(id+"F0.wireOp",EDGE,"E12.trimOffspring"),sQuery(id+"F0.wireOp",EDGE,"E13.1.0"),sQuery(id+"F0.wireOp",EDGE,"E13.2.0"),sQuery(id+"F0.wireOp",EDGE,"E13.3.0"),sQuery(id+"F0.wireOp",EDGE,"E13.4.0"),sQuery(id+"F0.wireOp",EDGE,"E13.5.0"),sQuery(id+"F0.wireOp",EDGE,"E13.6.0"),sQuery(id+"F0.wireOp",EDGE,"E13.7.0"),sQuery(id+"F0.wireOp",EDGE,"E13.8.0"),sQuery(id+"F0.wireOp",EDGE,"E13.9.0"),sQuery(id+"F0.wireOp",EDGE,"E14.trimOffspring"),sQuery(id+"F0.wireOp",EDGE,"E16.trimOffspring"),sQuery(id+"F0.wireOp",EDGE,"E18.trimOffspring"),sQuery(id+"F0.wireOp",EDGE,"E20.trimOffspring"),sQuery(id+"F0.wireOp",EDGE,"E22.trimOffspring"),sQuery(id+"F0.wireOp",EDGE,"E24.trimOffspring"),sQuery(id+"F0.wireOp",EDGE,"E26.trimOffspring"),sQuery(id+"F0.wireOp",EDGE,"E28.trimOffspring"),sQuery(id+"F0.wireOp",EDGE,"E30.trimOffspring")])],"isStart":false});
            var sketch = newSketch(context, id + "F5", { "sketchPlane" : qUnion([Q0])});
            skLineSegment(sketch, "E37.bottom", {"start": v(-4.04, 0) * mm, "end": v(4.18, 0) * mm});
            skLineSegment(sketch, "E37.top", {"start": v(-4.04, -3.64) * mm, "end": v(4.18, -3.64) * mm});
            skLineSegment(sketch, "E37.left", {"start": v(-4.04, 0) * mm, "end": v(-4.04, -3.64) * mm});
            skLineSegment(sketch, "E37.right", {"start": v(4.18, 0) * mm, "end": v(4.18, -3.64) * mm});
            skSolve(sketch);
        }
        {
            var Q0;
            Q0 = qSketchRegion(id + "F5", true);
            extrude(context, id + "F6", {"entities" : qUnion([Q0]), "operationType" : NewBodyOperationType.REMOVE, "oppositeDirection" : true, "depth" : 25 * mm});
        }
    });
